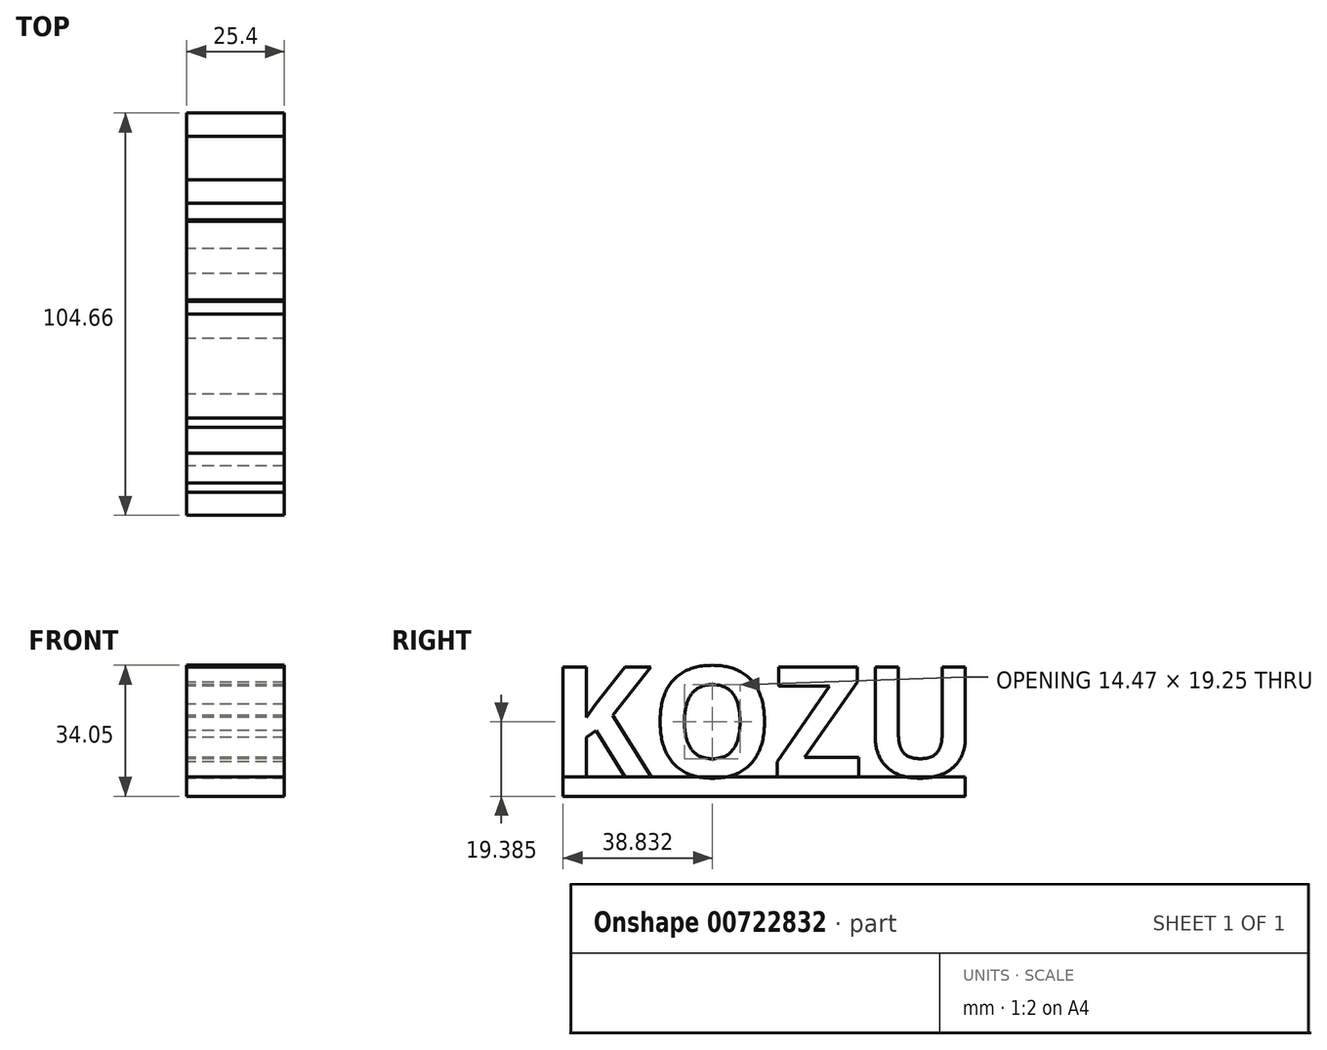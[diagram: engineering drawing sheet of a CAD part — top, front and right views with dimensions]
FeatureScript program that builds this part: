
annotation { "Feature Type Name" : "Feature", "Feature Type Description" : "" }
export const myFeature = defineFeature(function(context is Context, id is Id, definition is map)
    precondition{}
    {
        {
            var Q0;
            Q0=qCreatedBy(makeId("Right.planeOp"),FACE);
            var sketch = newSketch(context, id + "F0", { "sketchPlane" : qUnion([Q0])});
            skText(sketch, "E0", { "text": "KOZU", "fontName": "OpenSans-Bold.ttf"});
            const initialGuessF0  = {"E0": [-0.0412, -0.01208, 1, 0, 0.02876]};
            skSetInitialGuess(sketch, initialGuessF0);
            skSolve(sketch);
        }
        {
            var Q0;
            Q0 = qSketchRegion(id + "F0", true);
            extrude(context, id + "F1", {"entities" : qUnion([Q0]), "depth" : 25.4 * mm, "offsetDistance" : 25.4 * mm});
        }
        {
            var Q0;
            Q0=makeQuery(id+"F1.opExtrude","SWEPT_FACE",FACE,{"disambiguationData":[OSD([sQuery(id+"F0.wireOp",EDGE,"E0.sketch_text.stroke-4")])]});
            var sketch = newSketch(context, id + "F2", { "sketchPlane" : qUnion([Q0])});
            skLineSegment(sketch, "E1.bottom", {"start": v(0, 37.61) * mm, "end": v(25.4, 37.61) * mm});
            skLineSegment(sketch, "E1.top", {"start": v(0, -67.04) * mm, "end": v(25.4, -67.04) * mm});
            skLineSegment(sketch, "E1.left", {"start": v(0, 37.61) * mm, "end": v(0, -67.04) * mm});
            skLineSegment(sketch, "E1.right", {"start": v(25.4, 37.61) * mm, "end": v(25.4, -67.04) * mm});
            skSolve(sketch);
        }
        {
            var Q0;
            Q0 = qSketchRegion(id + "F2", true);
            extrude(context, id + "F3", {"entities" : qUnion([Q0]), "depth" : 5.08 * mm, "offsetDistance" : 25.4 * mm});
        }
    });
